# Revit family: Gira_212000
name_source: partatom
category: Elektroinstallationen
revit_build: Autodesk Revit 2017 (Build: 20160225_1515(x64)
units: mm (PartAtom-declared; Revit-internal decimal feet)

## family parameters
Basisbauteil = Fläche
Beim Laden mit Abzugskörper schneiden = Nein
Bemaßung runder Anschluss = Durchmesser verwenden
Beschriftungsausrichtung beibehalten = Nein
Gemeinsam genutzt = Nein
Raumberechnungspunkt = Nein
Teiletyp = Normal

## types (1)
- Spannungsversorgung 160 mA Drossel KNX REG
    Andere Bussysteme = sonstige
    Anzahl der Ausgänge = 0
    Anzahl der Eingänge = 0
    Anzahl der binären Eingänge = 0
    BIM = https://media.stage.bim.site 8f.rfa
    BIMSITE_PRODUCT_ID = f22732c19fceb7285109560b0cfdd15072a671c7
    Beschreibung = KNX Spannungsversorgung 160 mA mit integrierter Drossel   Spannungsversorgungen zur Versorgung von KNX Geräten mit Busspannung.  Merkmale:  Ausgang mit integrierter Drossel zur Versorgung von KNX Buslinien.  Ausgang DC 30 V zur Versorgung zusätzlicher Geräte.  Nennstrom beliebig auf die Ausgänge aufteilbar.  Reset-Taster.  Kurzschlussfest.  Überspannungsfest.  Leerlaufsicher.  Geeignet für Betrieb in Anlagen mit Notstromversorgung.  Potenzialfreier Meldekontakt für Betriebs- und Diagnosemeldung.  Zwei typgleiche KNX Spannungsversorgungen zur Leistungserhöhung direkt parallel schaltbar.  Hinweise :  Montage auf DIN-Hutschiene.  VDE-Zulassung gemäß EN 60669-1, EN 60669-2-1.
    Blindleistung = Nein
    Breite in Teilungseinheiten = 4
    Busspannung pufferbar = Nein
    Bussystem Funkbus = Nein
    Bussystem KNX = Ja
    Bussystem KNX-Funk = Nein
    Bussystem LON = Nein
    Bussystem Powernet = Nein
    Datenblatt = https://media.stage.bim.site
    Datenblatt 1 = https://media.stage.bim.site
    Funktion Schalten = Nein
    GTIN = 4010337023210
    Geeignet für C-Last = Nein
    HAN = 212000
    Handschaltung = Nein
    HeinzeBIM = https://www.heinze.de
    Hersteller = Gira
    Kosten = 0 $
    LED ansteuern = Nein
    Max. Anzahl der Jalousieausgänge = 0
    Max. Anzahl der Schaltausgänge = 0
    Max. Ausgangsstrom = 0 A
    Max. Schaltstrom = 0 A
    Mit Busankopplung = Nein
    Mit LED-Anzeige = Nein
    Modulare Erweiterungsmöglichkeit = Nein
    Montageart = REG
    Produktseite = https://media.stage.bim.site
    Stellgröße schaltend = Nein
    Stellgröße stetig = Nein
    Tarifumschaltung = Nein
    Typname = Spannungsversorgung 160 mA Drossel KNX REG
    URL = https://www.gira.de
    Ventilschutzfunktion = Nein
    Verschiedene Phasen anschließbar = Nein
    Vor Ort-/Handbedienung = Nein
    Vorgabe-Ansicht = 1219 mm
    Zulassung nach PTB = Nein

## geometry (parser evidence)
native form markers: Sweep x3
no freeform markers — native parametric forms only
